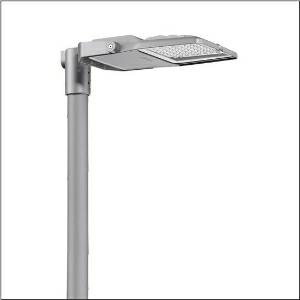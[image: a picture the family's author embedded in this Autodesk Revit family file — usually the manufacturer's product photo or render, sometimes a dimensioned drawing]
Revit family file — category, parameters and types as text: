
# Revit family: floodlight_fl_21_iq_mini___pl64_5xa7772b4e3a_29df
name_source: partatom
category: Lighting Fixtures
units: mm (PartAtom-declared; Revit-internal decimal feet)

## family parameters
Cut with Voids When Loaded = No
Host = Face
Light Source = No
Part Type = Normal
Room Calculation Point = No
Round Connector Dimension = Use Diameter
Shared = No

## types (1)
- --- (1 x LED, 6270 lm, 45.5 W, 4000K)
    Apparent Load = 46 VA
    CIE Flux Codes = 28 80 98 100 100
    Color Rendering = 70
    Color Temperature = 4000K
    Default Elevation = 1800 mm
    Description = Floodlight FL 21 iQ mini, floodlight, primary light control with lens, of PMMA, primary optical cover: protective disc, of toughened safety glass, transparent, light distribution: PL64, light emission: direct distribution, installation type: surface-mounted, LED, High Power LED, rated luminous flux: 6.270lm, luminous efficacy: 138lm/W, light colour: 740, colour temperature: 4000K, control gear: iQ Street-Remote/DALI, control: Auto-Match, Temp-Guard, Night-Set, Smart-Wire, Desk-Remote (wireless, voltage-free reading and setting of iQ features in the workshop via application-optimized NFC function/RFID function), optimised constant luminous flux control (CLO 2.0), Light-Fading, Lumen-Switch, with terminal, 6-pole, mains connection: 220..240V, AC, 50/60Hz, start of lifetime: 46W, end of service life: 48W, reduction: 22W, luminaire housing, of diecast aluminium, powder-coated, Siteco® metallic grey (DB 702S), corrosivity category C5 mid according to DIN EN ISO 12944, suitable for swimming pools, chlorine-resistant, sealing non-destructively replaceable, please order mast flange separately, mast bracket, of steel, galvanised, powder-coated, protection rating (complete): IP66, insulation class (complete): insulation class II (safety insulation), certification: CE, ENEC, VDE, protection symbol: D, impact resistance: IK08, permissible operating ambient temperature: -40..+40°C, permissible operating ambient temperature for outdoor applications: -40..+50°C, standard: DIN EN 12944, LABS conformity tested according to VDMA 24364:2018-05, packaging unit: 1 piece

Light Distribution: PL64
    Height = 70 mm
    Lamp = 1 x LED
    Lamp Light Flux = 6270 lm
    Lamp Power = 45.5 W
    Lamp count = 1
    Length = 485 mm
    Luminous efficacy = 138 lm/W
    Manufacturer = Siteco
    ModVariant = No
    Model = 5XA7772B4E3A
    Number of Poles = 1
    OnlyDefault = Yes
    Power Factor = 1
    Product Name = Floodlight FL 21 iQ mini | PL64
    Product group = floodlight | pylon annexe
    ProductGroupID = 6201
    Protection Class = Protection class II
    Protection Degree = IP 66
    RLX_Detail_Level = 1
    RLX_Emergency_Light_Flux = 0 lm
    RLX_Emergency_Type = 0
    RLX_Emergency_Type_DB = No
    RlxData = <blob elided: 101353 chars, md5=22fbab7f>
    Socket = socket
    Standby Power = 0 W
    System Light Flux = 6270 lm
    System Power = 46 W
    Type Comments = factory setting: luminous flux: 100 % | dim-lin: 254 | 463 mA
    Type Image = l_1007125.jpg
    URL = http://relux.com
    VarID = @adj_188223
    Voltage = 0 V
    Weight = 0.00 kg
    Width = 337 mm

## geometry (parser evidence)
native form markers: Blend x4, Sweep x12
no freeform markers — native parametric forms only
